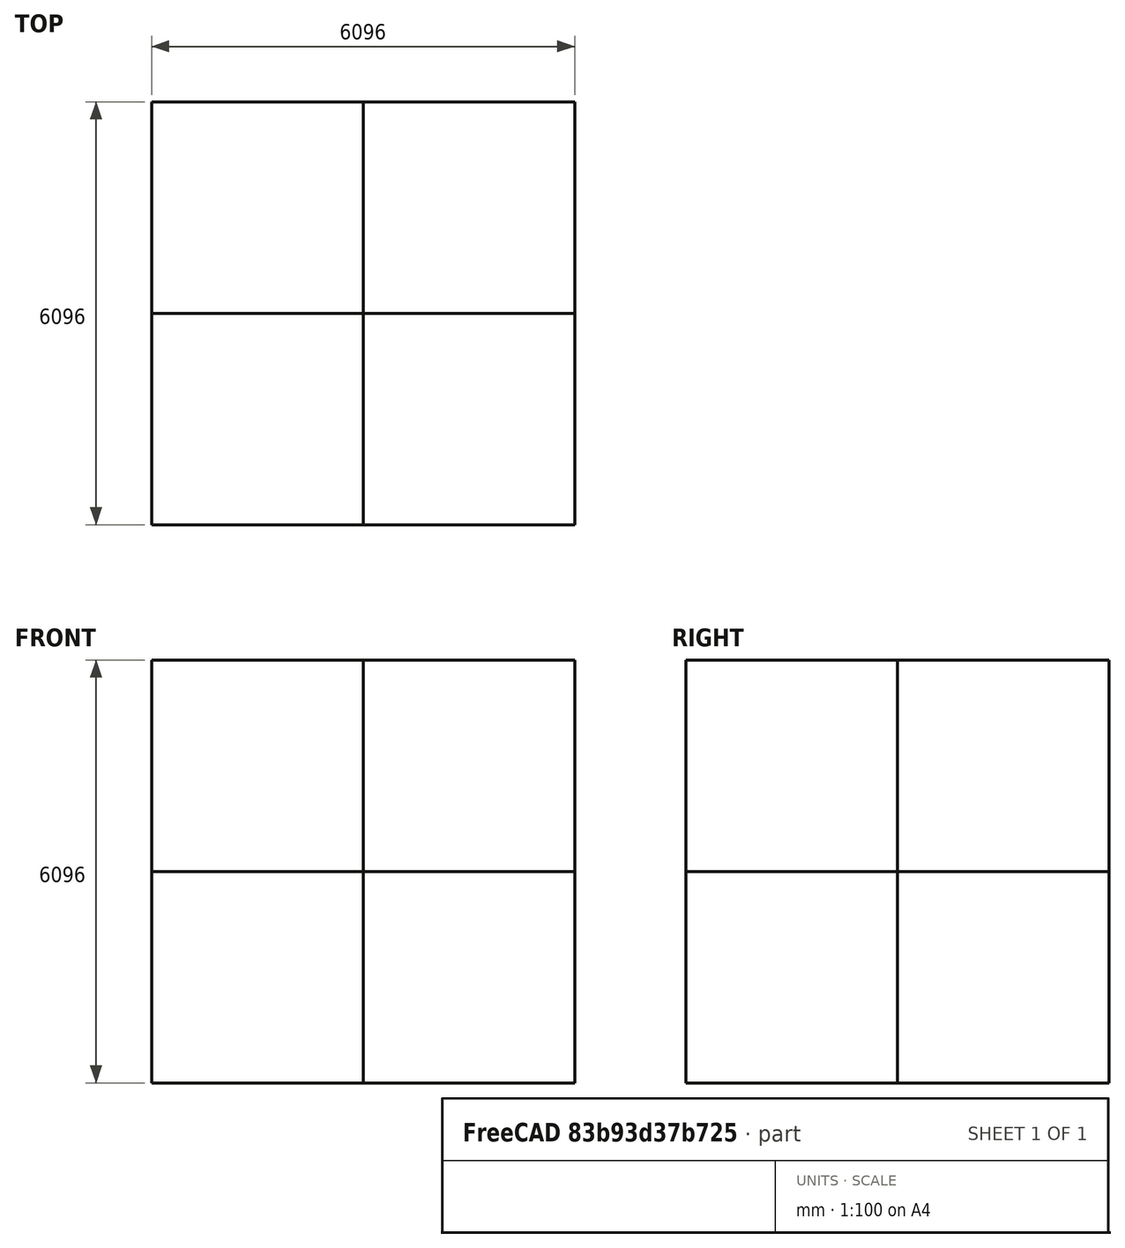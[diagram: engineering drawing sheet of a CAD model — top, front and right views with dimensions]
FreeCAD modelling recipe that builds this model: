
FCSTD DOCUMENT  (FreeCAD 0.19R16466 (Git))
Label: Rooms_03
License: All rights reserved
LicenseURL: http://en.wikipedia.org/wiki/All_rights_reserved
objects: Part::FeaturePython×9, Part::Part2DObjectPython×8, Part::Extrusion×8, App::GeometryPython×3
note: 28 computed .brp shape members not serialized (recipe doc carries the construction recipe); baked Part::Feature solids carry a one-line shape summary decoded from their .brp

FEATURE [Part::Part2DObjectPython] Wire  # Draft 2D object (typed FeaturePython)
  ChamferSize = 0
  Closed = true
  End = (3048,3048,0)
  FilletRadius = 0
  Length = 12192
  MakeFace = true
  Points = (4) [(0,3048,0),(0,6096,0),(3048,6096,0),(3048,3048,0)]
  Start = (0,3048,0)
  Subdivisions = 0
FEATURE [Part::Extrusion] __body
  Base = -> Wire
  Dir = (0,0,3048)
  DirMode = 0
  FaceMakerClass = Part::FaceMakerBullseye
  LengthFwd = 0
  LengthRev = 0
  Solid = false
  Symmetric = false
FEATURE [Part::FeaturePython] Space  label="2"  # Arch/BIM 114 (typed FeaturePython)
  Area = 9.2903e+06
  AutoPower = false
  Base = -> __body
  CompositionType = 1
  Conditioning = 0
  Description = TESTY
  ElevationWithFlooring = 0
  EquipmentPower = 0
  FloorThickness = 0
  HorizontalArea = 0
  IfcData = IfcUID=114zN7EpT7m88UZ_jczAhV,+1 more (map truncated)
  IfcProperties = Category;;Pset_ProductRequirements=IfcLabel;;Rooms,Category;;Pset_SpaceCommon=IfcLabel;;Rooms,CeilingCovering;;Pset_SpaceCommon=IfcLabel;;TESTY,+5 more (map truncated)
  IfcType = 114
  Internal = true
  LightingPower = 0
  LongName = TEST1A
  MoveBase = false
  MoveWithHost = true
  NumberOfPeople = 0
  PerimeterLength = 12192
  PredefinedType = 3
  SpaceType = 0
  VerticalArea = 3.71612e+07
FEATURE [Part::Part2DObjectPython] Wire001  # Draft 2D object (typed FeaturePython)
  ChamferSize = 0
  Closed = true
  End = (3048,3048,0)
  FilletRadius = 0
  Length = 12192
  MakeFace = true
  Points = (4) [(3048,6096,0),(6096,6096,0),(6096,3048,0),(3048,3048,0)]
  Start = (3048,6096,0)
  Subdivisions = 0
FEATURE [Part::Extrusion] __body001
  Base = -> Wire001
  Dir = (0,0,3048)
  DirMode = 0
  FaceMakerClass = Part::FaceMakerBullseye
  LengthFwd = 0
  LengthRev = 0
  Solid = false
  Symmetric = false
FEATURE [Part::FeaturePython] Space001  label="3"  # Arch/BIM 114 (typed FeaturePython)
  Area = 9290304
  AutoPower = false
  Base = -> __body001
  CompositionType = 1
  Conditioning = 0
  Description = TESTY
  ElevationWithFlooring = 0
  EquipmentPower = 0
  FloorThickness = 0
  HorizontalArea = 0
  IfcData = IfcUID=114zN7EpT7m88UZ_jczAh1,+1 more (map truncated)
  IfcProperties = Category;;Pset_ProductRequirements=IfcLabel;;Rooms,Category;;Pset_SpaceCommon=IfcLabel;;Rooms,CeilingCovering;;Pset_SpaceCommon=IfcLabel;;TESTY,+5 more (map truncated)
  IfcType = 114
  Internal = true
  LightingPower = 0
  LongName = TEST1B
  MoveBase = false
  MoveWithHost = true
  NumberOfPeople = 0
  PerimeterLength = 12192
  PredefinedType = 3
  SpaceType = 0
  VerticalArea = 37161216
FEATURE [Part::Part2DObjectPython] Wire002  # Draft 2D object (typed FeaturePython)
  ChamferSize = 0
  Closed = true
  End = (6096,3048,0)
  FilletRadius = 0
  Length = 12192
  MakeFace = true
  Points = (4) [(6096,0,0),(3048,0,0),(3048,3048,0),(6096,3048,0)]
  Start = (6096,0,0)
  Subdivisions = 0
FEATURE [Part::Extrusion] __body002
  Base = -> Wire002
  Dir = (0,0,3048)
  DirMode = 0
  FaceMakerClass = Part::FaceMakerBullseye
  LengthFwd = 0
  LengthRev = 0
  Solid = false
  Symmetric = false
FEATURE [Part::FeaturePython] Space002  label="4"  # Arch/BIM 114 (typed FeaturePython)
  Area = 9290304
  AutoPower = false
  Base = -> __body002
  CompositionType = 1
  Conditioning = 0
  Description = TESTY
  ElevationWithFlooring = 0
  EquipmentPower = 0
  FloorThickness = 0
  HorizontalArea = 0
  IfcData = IfcUID=114zN7EpT7m88UZ_jczAh3,+1 more (map truncated)
  IfcProperties = Category;;Pset_ProductRequirements=IfcLabel;;Rooms,Category;;Pset_SpaceCommon=IfcLabel;;Rooms,CeilingCovering;;Pset_SpaceCommon=IfcLabel;;TESTY,+5 more (map truncated)
  IfcType = 114
  Internal = true
  LightingPower = 0
  LongName = TEST1D
  MoveBase = false
  MoveWithHost = true
  NumberOfPeople = 0
  PerimeterLength = 12192
  PredefinedType = 3
  SpaceType = 0
  VerticalArea = 37161216
FEATURE [Part::Part2DObjectPython] Wire003  # Draft 2D object (typed FeaturePython)
  ChamferSize = 0
  Closed = true
  End = (3048,3048,0)
  FilletRadius = 0
  Length = 12192
  MakeFace = true
  Points = (4) [(3048,-1.9984e-11,0),(0,-1.9984e-11,0),(0,3048,0),(3048,3048,0)]
  Start = (3048,-1.9984e-11,0)
  Subdivisions = 0
FEATURE [Part::Extrusion] __body003
  Base = -> Wire003
  Dir = (0,0,3048)
  DirMode = 0
  FaceMakerClass = Part::FaceMakerBullseye
  LengthFwd = 0
  LengthRev = 0
  Solid = false
  Symmetric = false
FEATURE [Part::FeaturePython] Space003  label="5"  # Arch/BIM 114 (typed FeaturePython)
  Area = 9.2903e+06
  AutoPower = false
  Base = -> __body003
  CompositionType = 1
  Conditioning = 0
  Description = TESTY
  ElevationWithFlooring = 0
  EquipmentPower = 0
  FloorThickness = 0
  HorizontalArea = 0
  IfcData = IfcUID=114zN7EpT7m88UZ_jczAh5,+1 more (map truncated)
  IfcProperties = Category;;Pset_ProductRequirements=IfcLabel;;Rooms,Category;;Pset_SpaceCommon=IfcLabel;;Rooms,CeilingCovering;;Pset_SpaceCommon=IfcLabel;;TESTY,+5 more (map truncated)
  IfcType = 114
  Internal = true
  LightingPower = 0
  LongName = TEST1C
  MoveBase = false
  MoveWithHost = true
  NumberOfPeople = 0
  PerimeterLength = 12192
  PredefinedType = 3
  SpaceType = 0
  VerticalArea = 3.71612e+07
FEATURE [App::GeometryPython] BuildingPart001  label="Level 1"  # Arch/BIM 14 (typed FeaturePython)
  Area = 0
  CompositionType = 1
  Elevation = 0
  Group = -> [Space,Space001,Space002,Space003]
  Height = 0
  IfcData = IfcUID=1axJOFyDH0b9VOX55T$6zo,+1 more (map truncated)
  IfcProperties = AboveGround;;Pset_BuildingStoreyCommon=IfcLogical;;False,Category;;Pset_ProductRequirements=IfcLabel;;Levels,+2 more (map truncated)
  IfcType = 14
  LevelOffset = 0
  LongName = Level 1
  expr: Elevation = Placement.Base.z
FEATURE [Part::Part2DObjectPython] Wire004  # Draft 2D object (typed FeaturePython)
  ChamferSize = 0
  Closed = true
  End = (3048,3048,3048)
  FilletRadius = 0
  Length = 12192
  MakeFace = true
  Points = (4) [(0,3048,3048),(0,6096,3048),(3048,6096,3048),(3048,3048,3048)]
  Start = (0,3048,3048)
  Subdivisions = 0
FEATURE [Part::Extrusion] __body004
  Base = -> Wire004
  Dir = (0,0,3048)
  DirMode = 0
  FaceMakerClass = Part::FaceMakerBullseye
  LengthFwd = 0
  LengthRev = 0
  Solid = false
  Symmetric = false
FEATURE [Part::FeaturePython] Space004  label="6"  # Arch/BIM 114 (typed FeaturePython)
  Area = 9.2903e+06
  AutoPower = false
  Base = -> __body004
  CompositionType = 1
  Conditioning = 0
  Description = TESTY
  ElevationWithFlooring = 0
  EquipmentPower = 0
  FloorThickness = 0
  HorizontalArea = 0
  IfcData = IfcUID=114zN7EpT7m88UZ_jczAft,+1 more (map truncated)
  IfcProperties = Category;;Pset_ProductRequirements=IfcLabel;;Rooms,Category;;Pset_SpaceCommon=IfcLabel;;Rooms,CeilingCovering;;Pset_SpaceCommon=IfcLabel;;TESTY,+5 more (map truncated)
  IfcType = 114
  Internal = true
  LightingPower = 0
  LongName = TEST2A
  MoveBase = false
  MoveWithHost = true
  NumberOfPeople = 0
  PerimeterLength = 12192
  PredefinedType = 3
  SpaceType = 0
  VerticalArea = 3.71612e+07
FEATURE [Part::Part2DObjectPython] Wire005  # Draft 2D object (typed FeaturePython)
  ChamferSize = 0
  Closed = true
  End = (3048,3048,3048)
  FilletRadius = 0
  Length = 12192
  MakeFace = true
  Points = (4) [(3048,6096,3048),(6096,6096,3048),(6096,3048,3048),(3048,3048,3048)]
  Start = (3048,6096,3048)
  Subdivisions = 0
FEATURE [Part::Extrusion] __body005
  Base = -> Wire005
  Dir = (0,0,3048)
  DirMode = 0
  FaceMakerClass = Part::FaceMakerBullseye
  LengthFwd = 0
  LengthRev = 0
  Solid = false
  Symmetric = false
FEATURE [Part::FeaturePython] Space005  label="7"  # Arch/BIM 114 (typed FeaturePython)
  Area = 9290304
  AutoPower = false
  Base = -> __body005
  CompositionType = 1
  Conditioning = 0
  Description = TESTY
  ElevationWithFlooring = 0
  EquipmentPower = 0
  FloorThickness = 0
  HorizontalArea = 0
  IfcData = IfcUID=114zN7EpT7m88UZ_jczAfw,+1 more (map truncated)
  IfcProperties = Category;;Pset_ProductRequirements=IfcLabel;;Rooms,Category;;Pset_SpaceCommon=IfcLabel;;Rooms,CeilingCovering;;Pset_SpaceCommon=IfcLabel;;TESTY,+5 more (map truncated)
  IfcType = 114
  Internal = true
  LightingPower = 0
  LongName = TEST2B
  MoveBase = false
  MoveWithHost = true
  NumberOfPeople = 0
  PerimeterLength = 12192
  PredefinedType = 3
  SpaceType = 0
  VerticalArea = 37161216
FEATURE [Part::Part2DObjectPython] Wire006  # Draft 2D object (typed FeaturePython)
  ChamferSize = 0
  Closed = true
  End = (6096,3048,3048)
  FilletRadius = 0
  Length = 12192
  MakeFace = true
  Points = (4) [(6096,0,3048),(3048,0,3048),(3048,3048,3048),(6096,3048,3048)]
  Start = (6096,0,3048)
  Subdivisions = 0
FEATURE [Part::Extrusion] __body006
  Base = -> Wire006
  Dir = (0,0,3048)
  DirMode = 0
  FaceMakerClass = Part::FaceMakerBullseye
  LengthFwd = 0
  LengthRev = 0
  Solid = false
  Symmetric = false
FEATURE [Part::FeaturePython] Space006  label="8"  # Arch/BIM 114 (typed FeaturePython)
  Area = 9290304
  AutoPower = false
  Base = -> __body006
  CompositionType = 1
  Conditioning = 0
  Description = TESTY
  ElevationWithFlooring = 0
  EquipmentPower = 0
  FloorThickness = 0
  HorizontalArea = 0
  IfcData = IfcUID=114zN7EpT7m88UZ_jczAfy,+1 more (map truncated)
  IfcProperties = Category;;Pset_ProductRequirements=IfcLabel;;Rooms,Category;;Pset_SpaceCommon=IfcLabel;;Rooms,CeilingCovering;;Pset_SpaceCommon=IfcLabel;;TESTY,+5 more (map truncated)
  IfcType = 114
  Internal = true
  LightingPower = 0
  LongName = TEST2D
  MoveBase = false
  MoveWithHost = true
  NumberOfPeople = 0
  PerimeterLength = 12192
  PredefinedType = 3
  SpaceType = 0
  VerticalArea = 37161216
FEATURE [Part::Part2DObjectPython] Wire007  # Draft 2D object (typed FeaturePython)
  ChamferSize = 0
  Closed = true
  End = (3048,3048,3048)
  FilletRadius = 0
  Length = 12192
  MakeFace = true
  Points = (4) [(3048,-1.9984e-11,3048),(0,-1.9984e-11,3048),(0,3048,3048),(3048,3048,3048)]
  Start = (3048,-1.9984e-11,3048)
  Subdivisions = 0
FEATURE [Part::Extrusion] __body007
  Base = -> Wire007
  Dir = (0,0,3048)
  DirMode = 0
  FaceMakerClass = Part::FaceMakerBullseye
  LengthFwd = 0
  LengthRev = 0
  Solid = false
  Symmetric = false
FEATURE [Part::FeaturePython] Space007  label="9"  # Arch/BIM 114 (typed FeaturePython)
  Area = 9.2903e+06
  AutoPower = false
  Base = -> __body007
  CompositionType = 1
  Conditioning = 0
  Description = TESTY
  ElevationWithFlooring = 0
  EquipmentPower = 0
  FloorThickness = 0
  HorizontalArea = 0
  IfcData = IfcUID=114zN7EpT7m88UZ_jczAf_,+1 more (map truncated)
  IfcProperties = Category;;Pset_ProductRequirements=IfcLabel;;Rooms,Category;;Pset_SpaceCommon=IfcLabel;;Rooms,CeilingCovering;;Pset_SpaceCommon=IfcLabel;;TESTY,+5 more (map truncated)
  IfcType = 114
  Internal = true
  LightingPower = 0
  LongName = TEST2C
  MoveBase = false
  MoveWithHost = true
  NumberOfPeople = 0
  PerimeterLength = 12192
  PredefinedType = 3
  SpaceType = 0
  VerticalArea = 3.71612e+07
FEATURE [App::GeometryPython] BuildingPart002  label="Level 2"  # Arch/BIM 14 (typed FeaturePython)
  Area = 0
  CompositionType = 1
  Elevation = 3048
  Group = -> [Space004,Space005,Space006,Space007]
  Height = 0
  IfcData = IfcUID=1axJOFyDH0b9VOX55T$6Jx,+1 more (map truncated)
  IfcProperties = AboveGround;;Pset_BuildingStoreyCommon=IfcLogical;;False,Category;;Pset_ProductRequirements=IfcLabel;;Levels,+2 more (map truncated)
  IfcType = 14
  LevelOffset = 0
  LongName = Level 2
  Placement = pos=(0,0,3048) rot=(0,0,1;0rad)
  expr: Elevation = Placement.Base.z
FEATURE [App::GeometryPython] BuildingPart  label="Building"  # Arch/BIM 11 (typed FeaturePython)
  Area = 0
  BuildingType = 0
  CompositionType = 1
  ElevationOfRefHeight = 0
  ElevationOfTerrain = 0
  Group = -> [BuildingPart001,BuildingPart002]
  Height = 0
  IfcData = IfcUID=1axJOFyDH0b9VOX56Y0v7W,+1 more (map truncated)
  IfcProperties = Category;;Pset_ProductRequirements=IfcLabel;;Project Information; IsLandmarked;;Pset_BuildingCommon=IfcLogical;;False; NumberOfStoreys;;Pset_BuildingCommon=IfcInteger;;0
  IfcType = 11
  LevelOffset = 0
FEATURE [Part::FeaturePython] Site  label="Default"  # Arch/BIM 109 (typed FeaturePython)
  AdditionVolume = 0
  Area = 0
  CompositionType = 1
  Declination = 0
  Elevation = 0
  ExtrusionVector = (0,0,-100000)
  Group = -> [BuildingPart]
  Height = 0
  IfcData = IfcUID=1axJOFyDH0b9VOX56Y0v7Z,+1 more (map truncated)
  IfcType = 109
  Latitude = 42.3583
  Longitude = -71.0597
  OriginOffset = (0,0,0)
  Perimeter = 0
  ProjectedArea = 0
  RefElevation = 0
  RemoveSplitter = false
  SubtractionVolume = 0
